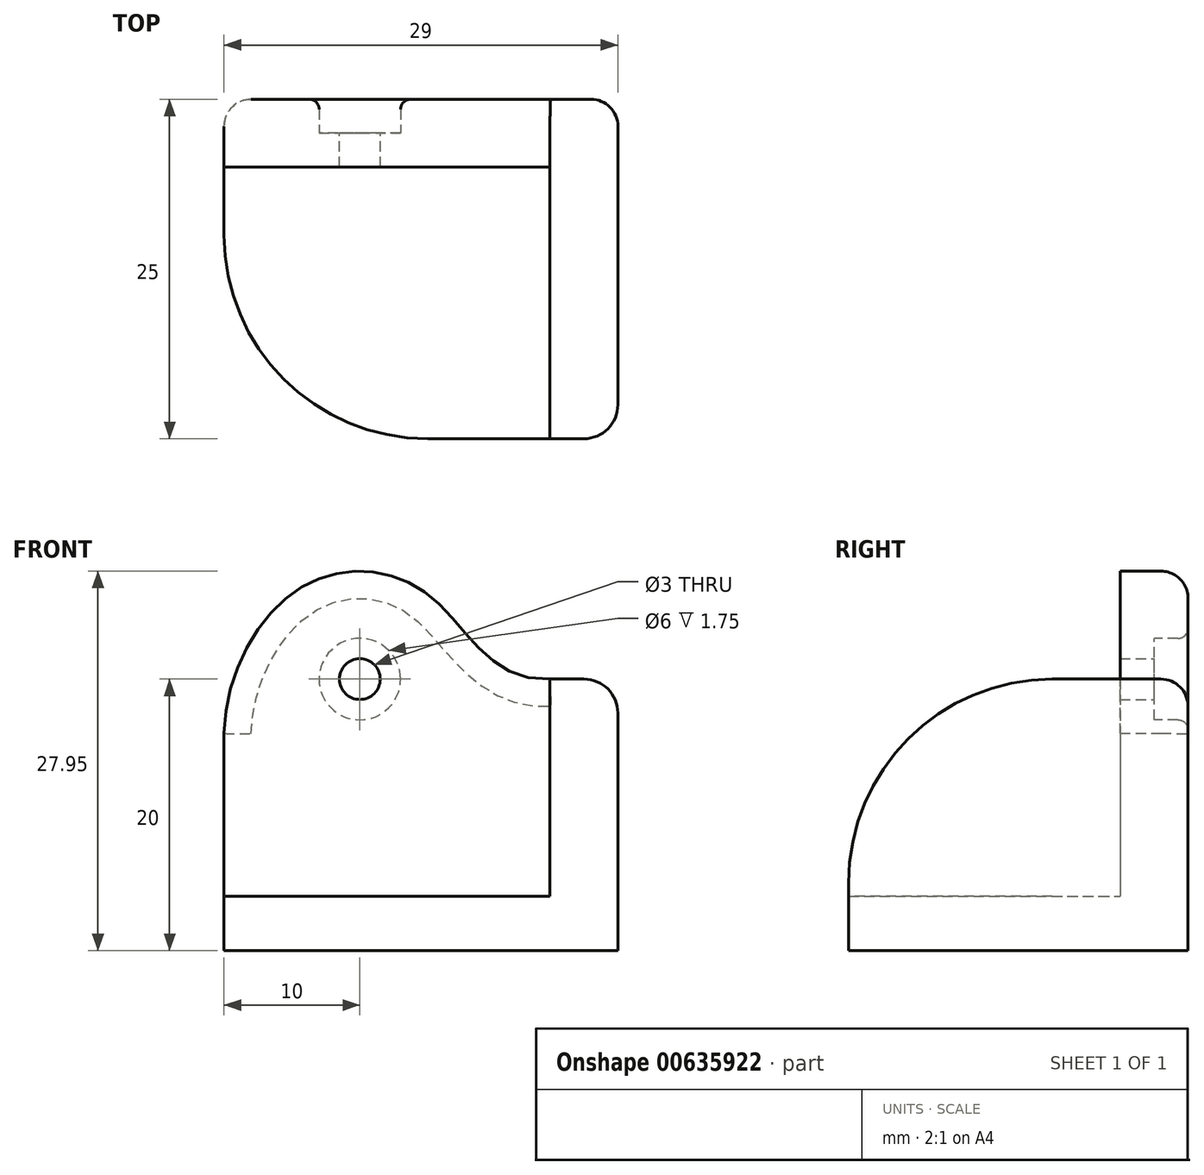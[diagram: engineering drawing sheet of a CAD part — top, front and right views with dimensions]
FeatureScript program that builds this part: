
annotation { "Feature Type Name" : "Feature", "Feature Type Description" : "" }
export const myFeature = defineFeature(function(context is Context, id is Id, definition is map)
    precondition{}
    {
        {
            var Q0;
            Q0=qCreatedBy(makeId("Front.planeOp"),FACE);
            var sketch = newSketch(context, id + "F0", { "sketchPlane" : qUnion([Q0])});
            skLineSegment(sketch, "E0.bottom", {"start": v(-24, 4) * mm, "end": v(0, 4) * mm});
            skLineSegment(sketch, "E0.top", {"start": v(-24, 0) * mm, "end": v(0, 0) * mm});
            skLineSegment(sketch, "E0.left", {"start": v(-24, 4) * mm, "end": v(-24, 0) * mm});
            skLineSegment(sketch, "E0.right", {"start": v(0, 4) * mm, "end": v(0, 0) * mm});
            skLineSegment(sketch, "E1.bottom", {"start": v(0, 20) * mm, "end": v(5, 20) * mm});
            skLineSegment(sketch, "E1.top", {"start": v(0, 0) * mm, "end": v(5, 0) * mm});
            skLineSegment(sketch, "E1.left", {"start": v(0, 20) * mm, "end": v(0, 0) * mm});
            skLineSegment(sketch, "E1.right", {"start": v(5, 20) * mm, "end": v(5, 0) * mm});
            skCircle(sketch, "E2", {"center": v(-14, 20) * mm, "radius": 1.5 * mm});
            skCircle(sketch, "E3", {"center": v(-14, 20) * mm, "radius": 3 * mm});
            skLineSegment(sketch, "E4", {"start": v(-24, 4) * mm, "end": v(-24, 16) * mm});
            skFitSpline(sketch, "E5", {"points": [v(-24, 16) * mm, v(-17.97, 26.95) * mm, v(-8.92, 26.18) * mm, v(0, 20) * mm], "startDerivative": vector(0.76, 38.3) * mm, "endDerivative": vector(40.23, 2.38) * mm});
            skSolve(sketch);
        }
        {
            var Q0;
            {var subQ0=sQuery(id+"F0.wireOp",EDGE,"E0.bottom");Q0=makeQuery(id+"F0.imprint","IMPRINT",FACE,{"disambiguationData":[TD([[makeQuery(id+"F0.imprint","IMPRINT",EDGE,{"derivedFrom":subQ0}),-1.0]])]});}
            var Q1;
            {var subQ3=sQuery(id+"F0.wireOp",EDGE,"E1.bottom");Q1=makeQuery(id+"F0.imprint","IMPRINT",FACE,{"disambiguationData":[TD([[makeQuery(id+"F0.imprint","IMPRINT",EDGE,{"derivedFrom":subQ3}),-1.0]])]});}
            extrude(context, id + "F1", {"entities" : qUnion([Q0, Q1]), "depth" : 25 * mm, "offsetDistance" : 25.4 * mm});
        }
        {
            var Q0;
            Q0 = qSketchRegion(id + "F0", true);
            var Q1;
            Q1=makeQuery(id+"F0.imprint","IMPRINT",FACE,{"disambiguationData":[TD([[makeQuery(id+"F0.imprint","IMPRINT",EDGE,{"derivedFrom":sQuery(id+"F0.wireOp",EDGE,"E2")}),-1.0]])]});
            extrude(context, id + "F2", {"entities" : qUnion([Q0, Q1]), "operationType" : NewBodyOperationType.ADD, "depth" : 5 * mm, "offsetDistance" : 25.4 * mm});
        }
        {
            var Q0;
            Q0=makeQuery(id+"F1.opExtrude","CAP_EDGE",EDGE,{"disambiguationData":[OSD([sQuery(id+"F0.wireOp",EDGE,"E0.left")])],"isStart":false});
            var Q1;
            Q1=makeQuery(id+"F1.opExtrude","CAP_EDGE",EDGE,{"disambiguationData":[OSD([sQuery(id+"F0.wireOp",EDGE,"E1.bottom")])],"isStart":false});
            fillet(context, id + "F3", {"entities" : qUnion([Q0, Q1]), "radius" : 15 * mm, "tangentPropagation" : true, "allowEdgeOverflow" : false});
        }
        {
            var Q0;
            Q0=makeQuery(id+"F1.opExtrude","SWEPT_EDGE",EDGE,{"disambiguationData":[OSD([sQuery(id+"F0.wireOp",EDGE,"E1.bottom"),sQuery(id+"F0.wireOp",EDGE,"E1.right")])]});
            fillet(context, id + "F4", {"entities" : qUnion([Q0]), "radius" : 2.5 * mm, "tangentPropagation" : true, "allowEdgeOverflow" : false});
        }
        {
            var Q0;
            Q0=makeQuery(id+"F0.imprint","IMPRINT",FACE,{"disambiguationData":[TD([[makeQuery(id+"F0.imprint","IMPRINT",EDGE,{"derivedFrom":sQuery(id+"F0.wireOp",EDGE,"E2")}),-1.0]])]});
            extrude(context, id + "F5", {"entities" : qUnion([Q0]), "operationType" : NewBodyOperationType.REMOVE, "endBound" : BoundingType.SYMMETRIC, "oppositeDirection" : true, "depth" : 5 * mm, "offsetDistance" : 25.4 * mm});
        }
        {
            var Q0;
            Q0=makeQuery(id+"F1.opExtrude","CAP_EDGE",EDGE,{"disambiguationData":[OSD([sQuery(id+"F0.wireOp",EDGE,"E1.right")])],"isStart":true});
            var Q1;
            {var subQ0=sQuery(id+"F0.wireOp",EDGE,"E1.right");var subQ1=sQuery(id+"F0.wireOp",EDGE,"E1.top");var subQ2=sQuery(id+"F0.wireOp",EDGE,"E1.bottom");var subQ3=sQuery(id+"F0.wireOp",EDGE,"E0.left");var subQ4=sQuery(id+"F0.wireOp",EDGE,"E0.top");Q1=makeQuery(id+"F4.opFillet","BLEND_EDGE",EDGE,{"blendedFrom":[makeQuery(id+"F1.opExtrude","SWEPT_EDGE",EDGE,{"disambiguationData":[OSD([subQ2,subQ0])]}),makeQuery(id+"F2.boolean.opBoolean","MERGE",FACE,{"derivedFrom":[makeQuery(id+"F1.opExtrude","CAP_FACE",FACE,{"disambiguationData":[OSD([sQuery(id+"F0.wireOp",EDGE,"E0.bottom"),subQ4,subQ3,subQ2,subQ1,sQuery(id+"F0.wireOp",EDGE,"E1.left"),subQ0])],"isStart":true}),makeQuery(id+"F2.opExtrude","CAP_FACE",FACE,{"disambiguationData":[OSD([subQ4,subQ3,subQ2,subQ1,subQ0,sQuery(id+"F0.wireOp",EDGE,"E2"),sQuery(id+"F0.wireOp",EDGE,"E4"),sQuery(id+"F0.wireOp",EDGE,"E5")])],"isStart":true})]})],"blendedInto":[makeQuery(id+"F2.boolean.opBoolean","MERGE",FACE,{"derivedFrom":[makeQuery(id+"F1.opExtrude","CAP_FACE",FACE,{"disambiguationData":[OSD([sQuery(id+"F0.wireOp",EDGE,"E0.bottom"),subQ4,subQ3,subQ2,subQ1,sQuery(id+"F0.wireOp",EDGE,"E1.left"),subQ0])],"isStart":true}),makeQuery(id+"F2.opExtrude","CAP_FACE",FACE,{"disambiguationData":[OSD([subQ4,subQ3,subQ2,subQ1,subQ0,sQuery(id+"F0.wireOp",EDGE,"E2"),sQuery(id+"F0.wireOp",EDGE,"E4"),sQuery(id+"F0.wireOp",EDGE,"E5")])],"isStart":true})]})]});}
            var Q2;
            {var subQ0=sQuery(id+"F0.wireOp",EDGE,"E0.left");Q2=makeQuery(id+"F2.boolean.opBoolean","MERGE",EDGE,{"derivedFrom":[makeQuery(id+"F1.opExtrude","CAP_EDGE",EDGE,{"disambiguationData":[OSD([subQ0])],"isStart":true}),makeQuery(id+"F2.opExtrude","CAP_EDGE",EDGE,{"disambiguationData":[OSD([subQ0,sQuery(id+"F0.wireOp",EDGE,"E4")])],"isStart":true})]});}
            var Q3;
            Q3=makeQuery(id+"F2.opExtrude","CAP_EDGE",EDGE,{"disambiguationData":[OSD([sQuery(id+"F0.wireOp",EDGE,"E5")])],"isStart":true});
            var Q4;
            Q4=makeQuery(id+"F1.opExtrude","CAP_EDGE",EDGE,{"disambiguationData":[OSD([sQuery(id+"F0.wireOp",EDGE,"E1.bottom")])],"isStart":true});
            fillet(context, id + "F6", {"entities" : qUnion([Q0, Q1, Q2, Q3, Q4]), "radius" : 2 * mm, "tangentPropagation" : true, "allowEdgeOverflow" : false});
        }
        {
            var Q0;
            {var subQ0=sQuery(id+"F0.wireOp",EDGE,"E1.right");var subQ1=sQuery(id+"F0.wireOp",EDGE,"E1.top");var subQ2=sQuery(id+"F0.wireOp",EDGE,"E1.bottom");var subQ3=sQuery(id+"F0.wireOp",EDGE,"E0.left");var subQ4=sQuery(id+"F0.wireOp",EDGE,"E0.top");Q0=makeQuery(id+"F5.boolean.opBoolean","INTERSECT",EDGE,{"derivedFrom":[makeQuery(id+"F2.boolean.opBoolean","MERGE",FACE,{"derivedFrom":[makeQuery(id+"F1.opExtrude","CAP_FACE",FACE,{"disambiguationData":[OSD([sQuery(id+"F0.wireOp",EDGE,"E0.bottom"),subQ4,subQ3,subQ2,subQ1,sQuery(id+"F0.wireOp",EDGE,"E1.left"),subQ0])],"isStart":true}),makeQuery(id+"F2.opExtrude","CAP_FACE",FACE,{"disambiguationData":[OSD([subQ4,subQ3,subQ2,subQ1,subQ0,sQuery(id+"F0.wireOp",EDGE,"E2"),sQuery(id+"F0.wireOp",EDGE,"E4"),sQuery(id+"F0.wireOp",EDGE,"E5")])],"isStart":true})]}),makeQuery(id+"F5.opExtrude","SWEPT_FACE",FACE,{"disambiguationData":[OSD([sQuery(id+"F0.wireOp",EDGE,"E3")])]})]});}
            fillet(context, id + "F7", {"entities" : qUnion([Q0]), "radius" : .75 * mm, "tangentPropagation" : true, "allowEdgeOverflow" : false});
        }
    });
